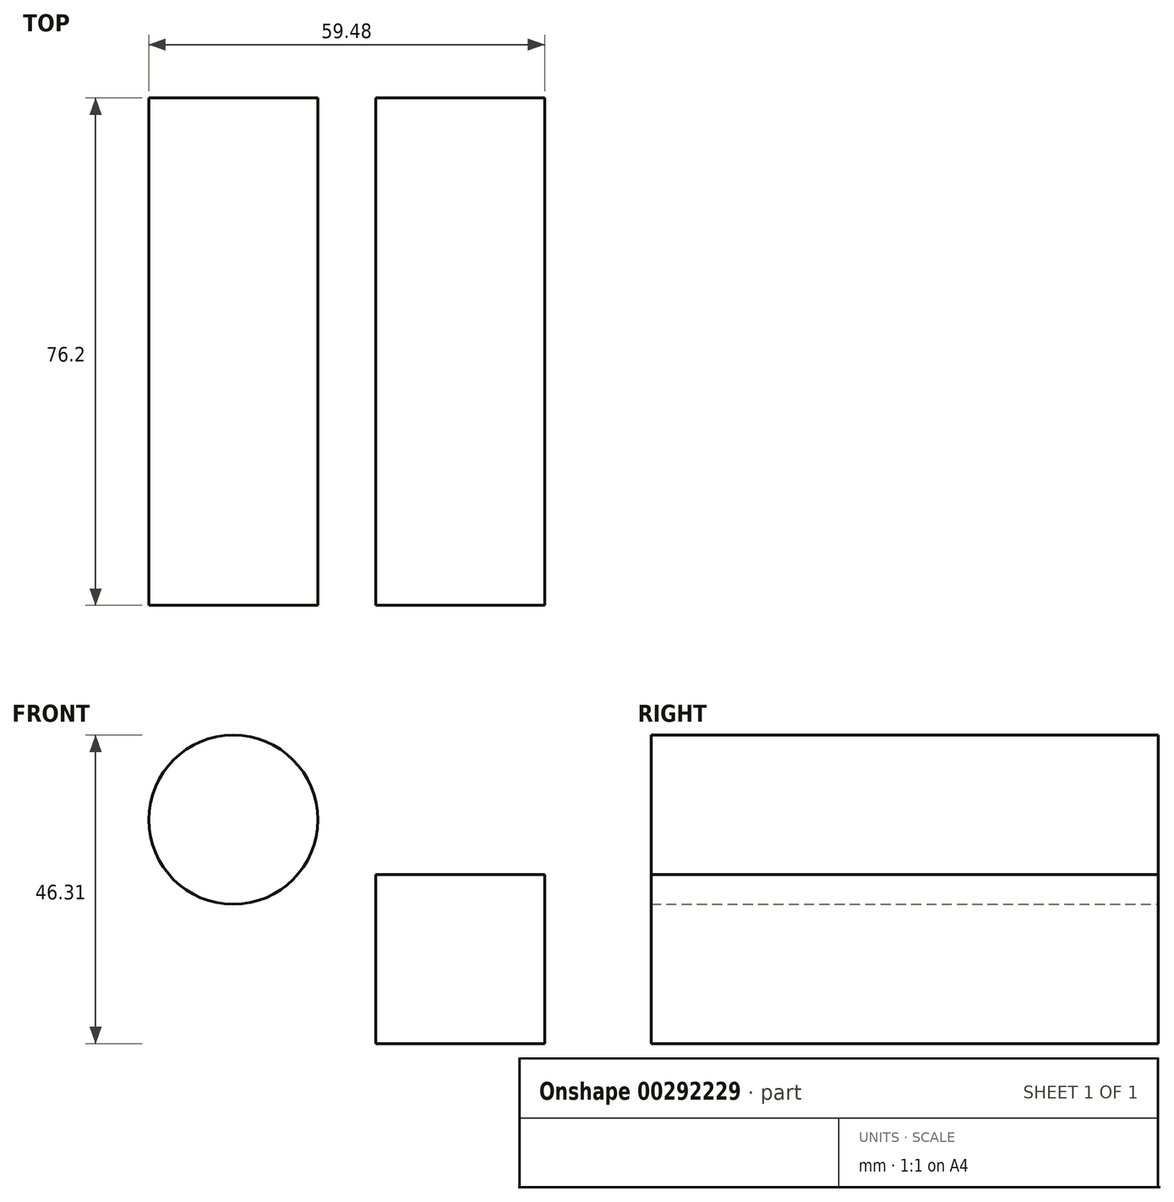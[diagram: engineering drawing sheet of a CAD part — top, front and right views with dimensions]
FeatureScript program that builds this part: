
annotation { "Feature Type Name" : "Feature", "Feature Type Description" : "" }
export const myFeature = defineFeature(function(context is Context, id is Id, definition is map)
    precondition{}
    {
        {
            var Q0;
            Q0=qCreatedBy(makeId("Front.planeOp"),FACE);
            var sketch = newSketch(context, id + "F0", { "sketchPlane" : qUnion([Q0])});
            skCircle(sketch, "E0", {"center": v(-64.16, 44.3) * mm, "radius": 12.7 * mm});
            skLineSegment(sketch, "E1.bottom", {"start": v(-42.78, 36.1) * mm, "end": v(-17.38, 36.1) * mm});
            skLineSegment(sketch, "E1.top", {"start": v(-42.78, 10.7) * mm, "end": v(-17.38, 10.7) * mm});
            skLineSegment(sketch, "E1.left", {"start": v(-42.78, 36.1) * mm, "end": v(-42.78, 10.7) * mm});
            skLineSegment(sketch, "E1.right", {"start": v(-17.38, 36.1) * mm, "end": v(-17.38, 10.7) * mm});
            skPoint(sketch, "E1.middle", {"position": v(-30.08, 23.4) * mm});
            skSolve(sketch);
        }
        {
            var Q0;
            Q0 = qSketchRegion(id + "F0", true);
            extrude(context, id + "F1", {"entities" : qUnion([Q0]), "depth" : 76.2 * mm});
        }
    });
